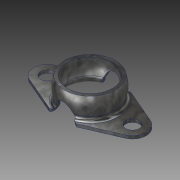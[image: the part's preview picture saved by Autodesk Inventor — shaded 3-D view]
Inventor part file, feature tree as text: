
AUTODESK INVENTOR PART (.ipt)
format: ipt  version: 2018 (Build 220112000, 112)  size: 342,016 bytes
history: native  units: in
note: dims shown in document units (in); Inventor stores cm internally (conversion verified against a paired STEP export)
features: extrude x1
ambient origin geometry x8: Origin, YZ Plane, XZ Plane, XY Plane, X Axis, Y Axis, Z Axis, Center Point
bodies: Solid1 (feature_tree)
feature tree (1):
  extrude  "Extrude5"  [1 undecoded]
note: 1 required parameter value undecoded (feature->parameter linkage not recoverable at this tier; creation-order binding heuristic only, values carry confidence <= 0.55)
